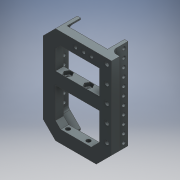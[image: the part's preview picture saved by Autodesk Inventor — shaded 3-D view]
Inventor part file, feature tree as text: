
AUTODESK INVENTOR PART (.ipt)
format: ipt  version: 2016 (Build 200138000, 138)  size: 514,560 bytes
history: native  units: mm
features: extrude x10, sketch x10, fillet x4, projected_geometry x1
ambient origin geometry x8: Origin, YZ Plane, XZ Plane, XY Plane, X Axis, Y Axis, Z Axis, Center Point
bodies: Body1 (feature_tree)
feature tree (25):
  extrude  "Extrusion2"  Depth=82.5mm
  extrude  "Extrusion7"  TaperAngle=135.0deg  [1 undecoded]
  extrude  "Extrusion8"  Depth=18.0mm
  extrude  "Extrusion9"  Depth=18.0mm
  extrude  "Extrusion17"  Depth=18.0mm
  extrude  "Extrusion18"  Depth=5.0mm
  extrude  "Extrusion19"  Depth=5.0mm
  fillet  "Fillet7"  Radius=11.625mm
  extrude  "Extrusion20"  Depth=9.0mm
  extrude  "Extrusion21"  Depth=45.5mm
  extrude  "Extrusion22"  Depth=18.0mm
  fillet  "Fillet8"  Radius=18.0mm
  fillet  "Fillet9"  Radius=18.0mm
  fillet  "Fillet10"  Radius=18.0mm
  sketch  "Sketch1"  dims[d1=142.5mm d3=82.5mm]
  sketch  "Sketch7"  dims[d4=60.0mm d5=135.0deg]
  sketch  "Sketch8"  dims[d6=120.0mm d8=18.0mm]
  sketch  "Sketch9"  dims[d10=18.0mm d11=18.0mm d17=18.0mm]
  sketch  "Sketch17"  dims[d20=18.0mm d21=18.0mm]
  sketch  "Sketch18"  dims[d22=12.0mm d23=0.0mm d47=5.0mm]
  projected_geometry  "Projected Loop3"
  sketch  "Sketch19"  dims[d48=5.0mm d49=5.0mm d50=11.625mm]
  sketch  "Sketch20"  dims[d51=11.625mm d52=9.0mm]
  sketch  "Sketch25"  dims[d54=0.0mm d55=0.0mm d58=45.5mm]
  sketch  "Sketch27"  dims[d59=45.5mm d61=18.0mm d63=18.0mm d65=18.0mm d66=18.0mm d68=135.0deg d73=45.0deg d74=18.0mm d75=36.0mm d76=64.5mm d77=64.5mm d78=45.0deg d79=106.5mm d80=45.5mm d81=6.0mm d82=6.0mm d83=15.0mm d84=6.0mm d85=15.0mm d86=6.0mm d87=88.5mm d88=0.0mm d90=11.625mm d91=6.0mm d92=7.0mm d93=12.5mm d94=6.0mm d95=25.0mm d96=6.0mm d97=25.0mm d98=6.0mm d99=25.0mm d100=6.0mm d101=25.0mm d102=88.5mm d103=0.0mm d170=10.4mm d171=10.4mm d172=5.0mm d173=0.0mm d174=5.0mm d175=25.0mm d176=0.0mm d177=10.4mm d178=10.4mm d179=10.4mm d180=10.4mm d181=10.4mm d182=5.0mm d183=0.0mm d184=8.0mm d185=5.0mm d186=5.0mm d187=5.0mm d188=5.0mm d190=5.0mm d192=5.0mm d193=20.0mm d194=0.0mm d232=71.25mm d233=5.0mm d234=6.0mm d235=6.0mm d236=5.0mm d237=5.0mm d238=5.0mm d239=5.0mm d240=5.0mm d241=5.0mm d242=5.0mm d243=12.0mm d244=12.0mm d245=12.0mm d246=12.0mm d247=12.0mm d248=12.0mm d249=12.0mm d250=5.0mm d251=0.0mm d252=5.0mm d253=6.0mm d254=6.0mm d255=5.0mm d256=5.0mm d257=5.0mm d258=5.0mm d259=5.0mm d260=12.0mm d261=12.0mm d262=12.0mm d263=12.0mm d264=12.0mm d265=5.0mm d266=5.0mm d267=5.0mm d268=5.0mm d269=12.0mm d270=12.0mm d271=12.0mm d272=12.0mm d273=12.0mm d274=6.0mm d275=5.0mm d276=0.0mm d277=8.0mm d278=8.0mm d279=8.0mm d280=5.0mm]
note: 1 required parameter value undecoded (feature->parameter linkage not recoverable at this tier; creation-order binding heuristic only, values carry confidence <= 0.55)
